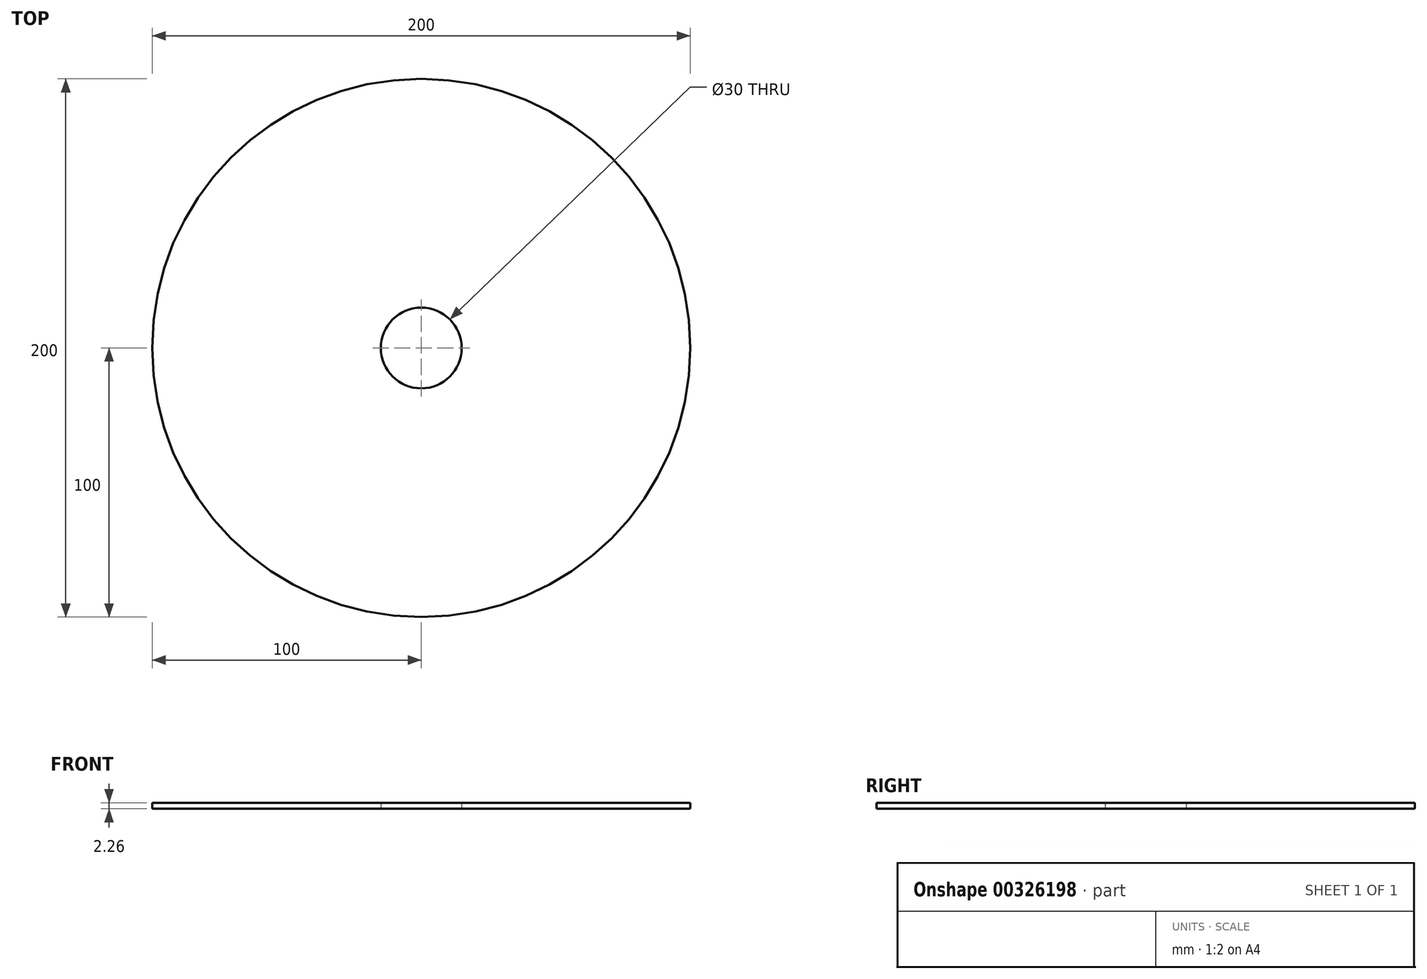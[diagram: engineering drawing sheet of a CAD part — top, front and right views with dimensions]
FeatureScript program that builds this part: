
annotation { "Feature Type Name" : "Feature", "Feature Type Description" : "" }
export const myFeature = defineFeature(function(context is Context, id is Id, definition is map)
    precondition{}
    {
        {
            var Q0;
            Q0=qCreatedBy(makeId("Top.planeOp"),FACE);
            var sketch = newSketch(context, id + "F0", { "sketchPlane" : qUnion([Q0])});
            skCircle(sketch, "E0", {"center": v(0, 0) * mm, "radius": 15 * mm});
            skCircle(sketch, "E1.0", {"center": v(0, 0) * mm, "radius": 100 * mm});
            skSolve(sketch);
        }
        {
            var Q0;
            Q0=makeQuery(id+"F0.imprint","IMPRINT",FACE,{"disambiguationData":[TD([[makeQuery(id+"F0.imprint","IMPRINT",EDGE,{"derivedFrom":sQuery(id+"F0.wireOp",EDGE,"E0")}),-1.0]])]});
            extrude(context, id + "F1", {"entities" : qUnion([Q0]), "endBound" : BoundingType.SYMMETRIC, "depth" : 2.25 * mm});
        }
    });
